# Revit family: 351_76166
name_source: partatom
category: Plumbing Fixtures
units: mm (PartAtom-declared; Revit-internal decimal feet)

## family parameters
Always vertical = Yes
Cut with Voids When Loaded = No
Part Type = Normal
Room Calculation Point = No
Round Connector Dimension = Use Diameter
Shared = No
Work Plane-Based = No

## types (1)
- 5650131 IDO GLOW SEINÄ-WC-ISTUIN
    CLBTZ = 0 mm  [stored 0 ft]
    CL_Location_5000 = 5000 mm  [stored 16.4042 ft]
    DC = 110 mm
    Description = WALL HUNG WC GLOW slow close seat
    H1 = 160 mm  [stored 0.524934 ft]
    H2 = 60 mm  [stored 0.19685 ft]
    H21 = 50 mm  [stored 0.164042 ft]
    H3 = 35 mm  [stored 0.114829 ft]
    H4 = 85 mm  [stored 0.278871 ft]
    H5 = 50 mm  [stored 0.164042 ft]
    H6 = 50 mm  [stored 0.164042 ft]
    L = 363 mm  [stored 1.19094 ft]
    L1 = 118 mm
    L2 = 124 mm  [stored 0.406824 ft]
    L21 = 133 mm  [stored 0.436352 ft]
    L3 = 145 mm  [stored 0.475722 ft]
    L4 = 155 mm  [stored 0.50853 ft]
    L5 = 167 mm  [stored 0.5479 ft]
    L6 = 180 mm  [stored 0.590551 ft]
    L7 = 182 mm
    QmdConnectorList = 601;DC
    URL = http://www.ido.fi
    W1 = 213 mm
    W2 = 212 mm  [stored 0.695538 ft]
    W21 = 228 mm  [stored 0.748031 ft]
    W4 = 280 mm  [stored 0.918635 ft]
    W5 = 304 mm  [stored 0.997375 ft]
    W6 = 320 mm  [stored 1.04987 ft]
    W7 = 344 mm
    XRefLineVPlnId = 7453
    YRefLineVPlnId = 7456
    magiPartTypeId = 351
    magiProductCode = 5650131 IDO GLOW SEINÄ-WC-ISTUIN
    magiProductFamilyId = 76166
    magiProductId = 76166

note: [stored X ft] marks values corroborated as IEEE doubles in the binary element streams (Revit-internal decimal feet)

## geometry (parser evidence)
native form markers: Sweep x2
no freeform markers — native parametric forms only
